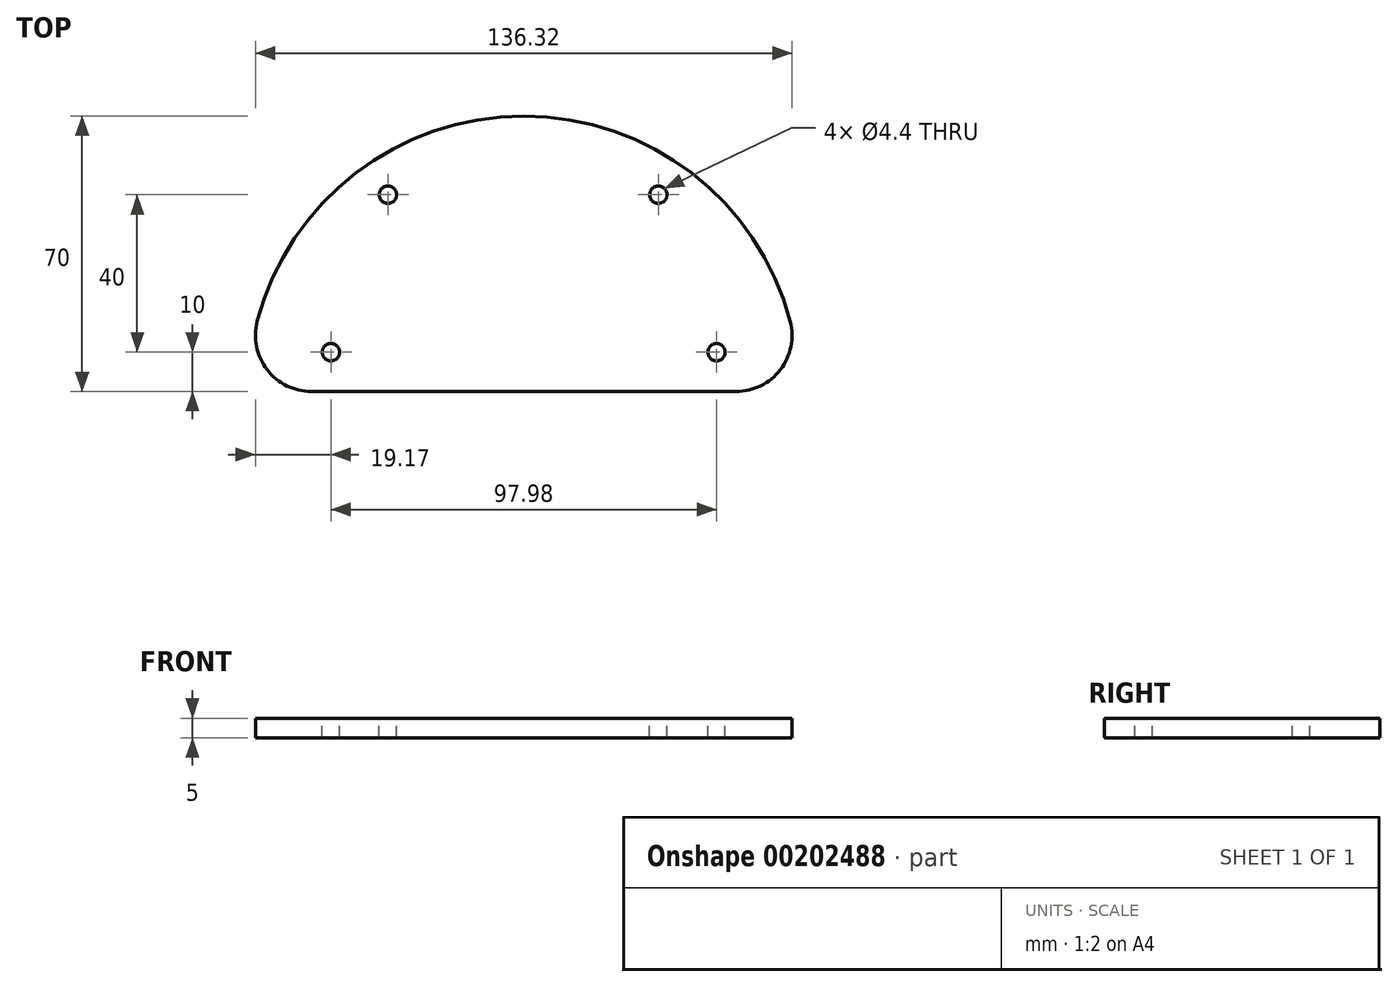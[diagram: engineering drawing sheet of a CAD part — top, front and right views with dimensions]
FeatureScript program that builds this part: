
annotation { "Feature Type Name" : "Feature", "Feature Type Description" : "" }
export const myFeature = defineFeature(function(context is Context, id is Id, definition is map)
    precondition{}
    {
        {
            var Q0;
            Q0=qCreatedBy(makeId("Top.planeOp"),FACE);
            var sketch = newSketch(context, id + "F0", { "sketchPlane" : qUnion([Q0])});
            skArc(sketch, "E0", {"start": v(70, 0) * mm, "mid": v(0, 70) * mm, "end": v(-70, 0) * mm});
            skLineSegment(sketch, "E1", {"start": v(-70, 0) * mm, "end": v(70, 0) * mm});
            skSolve(sketch);
        }
        {
            var Q0;
            Q0 = qSketchRegion(id + "F0", true);
            extrude(context, id + "F1", {"entities" : qUnion([Q0]), "depth" : 5 * mm});
        }
        {
            var Q0;
            Q0=makeQuery(id+"F1.opExtrude","CAP_FACE",FACE,{"disambiguationData":[OSD([sQuery(id+"F0.wireOp",EDGE,"E0"),sQuery(id+"F0.wireOp",EDGE,"E1")])],"isStart":false});
            var sketch = newSketch(context, id + "F2", { "sketchPlane" : qUnion([Q0])});
            skLineSegment(sketch, "E2", {"start": v(0, 70) * mm, "end": v(0, 0) * mm, "construction": true});
            skLineSegment(sketch, "E3", {"start": v(-48.99, 10) * mm, "end": v(48.99, 10) * mm, "construction": true});
            skLineSegment(sketch, "E4", {"start": v(-34.52, 50) * mm, "end": v(34.19, 50) * mm, "construction": true});
            skPoint(sketch, "E5", {"position": v(-34.52, 50) * mm});
            skPoint(sketch, "E6", {"position": v(34.19, 50) * mm});
            skPoint(sketch, "E7", {"position": v(48.99, 10) * mm});
            skPoint(sketch, "E8", {"position": v(-48.99, 10) * mm});
            skSolve(sketch);
        }
        {
            var Q0;
            Q0=sQuery(id+"F2.wireOp",VERTEX,"E5");
            var Q1;
            Q1=sQuery(id+"F2.wireOp",VERTEX,"E6");
            var Q2;
            Q2=sQuery(id+"F2.wireOp",VERTEX,"E7");
            var Q3;
            Q3=sQuery(id+"F2.wireOp",VERTEX,"E8");
            var Q4;
            Q4=makeQuery(id+"F1.opExtrude","SWEPT_BODY",BODY,{"disambiguationData":[OSD([sQuery(id+"F0.wireOp",EDGE,"E0"),sQuery(id+"F0.wireOp",EDGE,"E1")])]});
            hole(context, id + "F3", {"style" : HoleStyle.SIMPLE, "endStyle" : HoleEndStyle.THROUGH, "standardTappedOrClearance" : lookupTablePath({ "standard" : "ISO", "fit" : "Normal", "size" : "M4", "type" : "Clearance" }), "standardBlindInLast" : lookupTablePath({ "fit" : "Standard", "standard" : "ISO", "size" : "M4", "type" : "Clearance" }), "holeDiameter" : 4.4 * mm, "locations" : qUnion([Q0, Q1, Q2, Q3]), "scope" : qUnion([Q4]), "isTappedThrough" : true});
        }
        {
            var Q0;
            {var subQ0=sQuery(id+"F0.wireOp",EDGE,"E1");var subQ1=sQuery(id+"F0.wireOp",EDGE,"E0");Q0=makeQuery(id+"F1.opExtrude","SWEPT_EDGE",EDGE,{"disambiguationData":[OSD([subQ1,subQ0]),TDD([makeQuery(id+"F0.imprint","INTERSECT",VERTEX,{"disambiguationData":[OD(1.0)],"derivedFrom":[subQ1,subQ0]})])]});}
            var Q1;
            {var subQ0=sQuery(id+"F0.wireOp",EDGE,"E1");var subQ1=sQuery(id+"F0.wireOp",EDGE,"E0");Q1=makeQuery(id+"F1.opExtrude","SWEPT_EDGE",EDGE,{"disambiguationData":[OSD([subQ1,subQ0]),TDD([makeQuery(id+"F0.imprint","INTERSECT",VERTEX,{"disambiguationData":[OD(0.0)],"derivedFrom":[subQ1,subQ0]})])]});}
            fillet(context, id + "F4", {"entities" : qUnion([Q0, Q1]), "radius" : 14.22 * mm, "tangentPropagation" : true, "allowEdgeOverflow" : false});
        }
    });
